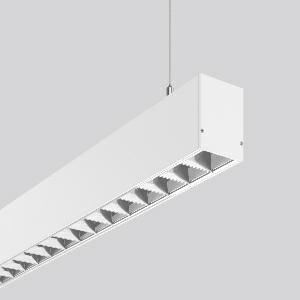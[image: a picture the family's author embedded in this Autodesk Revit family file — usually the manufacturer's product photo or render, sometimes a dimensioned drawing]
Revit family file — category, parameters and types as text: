
# Revit family: less_is_more_50_312337_002_672a
name_source: partatom
category: Lighting Fixtures
units: mm (PartAtom-declared; Revit-internal decimal feet)

## family parameters
Cut with Voids When Loaded = No
Host = Face
Light Source = No
Part Type = Normal
Room Calculation Point = No
Round Connector Dimension = Use Diameter
Shared = No

## types (1)
- LESS IS MORE 50 (1 x LED Modul 830, 4200 lm, 3000)
    Apparent Load = 35 VA
    CIE Flux Codes = 95 100 100 100 100
    Color Rendering = 80
    Color Temperature = 3000
    Default Elevation = 1800 mm
    Description = Series: LESS IS MORE 50
Linear pendant luminaire for aesthetically sophisticated lighting. Housing: extruded aluminium profile, powder-coated. End cap aluminium powder-coated. Canopy made of aluminium, powder-coated. Alea optical system: Reflector structure (ABS, Aluminium-coated, highly polished) with integrated diffuser made of non-yellowing plastic (PMMA) opal for glare-free light at the workstation (screen-compliant according to EN 12464-1). Direct light emission. Suitable for pendant. 2-point steel cable suspension freely positionable and infinitely height-adjustable. Special lengths available on request. LED unit with integrated converter interchangeable and removable. Suitable for through-wiring. With sensors or as a safety luminaire on request. 
Colour: traffic white, matt (RAL 9016)
Length: 1407 mm
Width: 57 mm
Height: 75 mm
Suspension length: 2000 mm
Lamp: LED
Socket: without socket
Colour temperature: 3000K
Colour rendering index (CRI): 80
System power: 35 W
Rated luminous flux: 4200 lm
Luminous efficiency: 120 lm/W
Control gear: Regulated power supply
Protection class: I
Type of protection: IP 20
    Height = 75 mm
    Lamp = 1 x LED Modul 830
    Lamp Light Flux = 4200 lm
    Lamp count = 1
    Length = 1407 mm
    Lifetime = 50000 h
    Luminous efficacy = 120 lm/W
    Manufacturer = RZB
    ModVariant = No
    Model = 312337.002
    Mounting Place = Ceiling
    Mounting Type = Pendant
    Number of Poles = 1
    OnlyDefault = Yes
    Power Factor = 1
    Product Name = LESS IS MORE 50
    Product group = Pendant LED linear luminaires
    ProductGroupID = 907
    Protection Class = Protection class I
    Protection Degree = IP 20
    RLX_Detail_Level = 1
    RLX_Emergency_Light_Flux = 0 lm
    RLX_Emergency_Type = 0
    RLX_Emergency_Type_DB = No
    RlxData = <blob elided: 33149 chars, md5=20e5952d>
    Socket = socket
    Standby Power = 0 W
    System Light Flux = 4200 lm
    System Power = 35 W
    Type Comments = Product without accessories
    Type Image = 312342.002.jpg
    URL = http://relux.com
    VarID = ---
    Voltage = 230 V
    Voltage Range = 220-240 V
    Weight = 0.00 kg
    Width = 57 mm

## geometry (parser evidence)
native form markers: Blend x4, Sweep x8
no freeform markers — native parametric forms only
